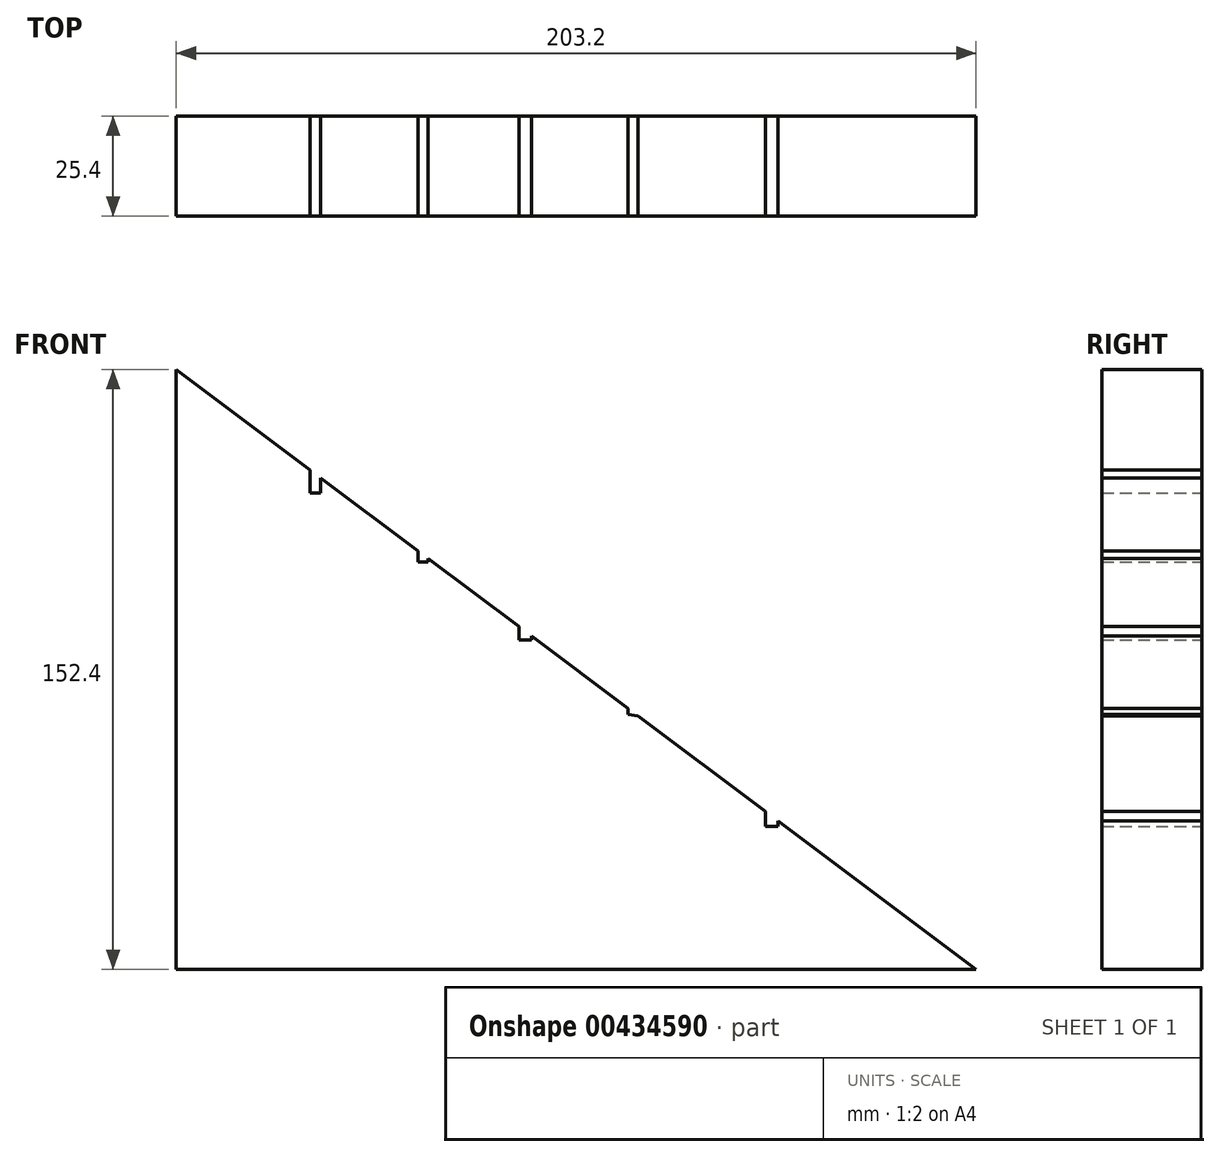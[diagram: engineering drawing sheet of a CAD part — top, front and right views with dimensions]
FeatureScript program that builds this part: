
annotation { "Feature Type Name" : "Feature", "Feature Type Description" : "" }
export const myFeature = defineFeature(function(context is Context, id is Id, definition is map)
    precondition{}
    {
        {
            var Q0;
            Q0=qCreatedBy(makeId("Front.planeOp"),FACE);
            var sketch = newSketch(context, id + "F0", { "sketchPlane" : qUnion([Q0])});
            skLineSegment(sketch, "E0", {"start": v(-68.59, 65.31) * mm, "end": v(-68.59, -87.09) * mm});
            skLineSegment(sketch, "E1", {"start": v(-68.59, -87.09) * mm, "end": v(134.61, -87.09) * mm});
            skLineSegment(sketch, "E2", {"start": v(-68.59, 65.31) * mm, "end": v(134.61, -87.09) * mm});
            skLineSegment(sketch, "E3", {"start": v(-68.59, -87.09) * mm, "end": v(81.12, -46.97) * mm});
            skLineSegment(sketch, "E4", {"start": v(-68.59, -87.09) * mm, "end": v(46.23, -20.8) * mm});
            skLineSegment(sketch, "E5", {"start": v(-68.59, -87.09) * mm, "end": v(18.5, 0) * mm});
            skLineSegment(sketch, "E6", {"start": v(-68.59, -87.09) * mm, "end": v(-7.19, 19.26) * mm});
            skLineSegment(sketch, "E7", {"start": v(-68.59, -87.09) * mm, "end": v(-34.59, 39.81) * mm});
            skLineSegment(sketch, "E8", {"start": v(-31.92, 34) * mm, "end": v(-31.92, 37.81) * mm});
            skLineSegment(sketch, "E9", {"start": v(-7.19, 19.26) * mm, "end": v(-7.19, 16.45) * mm});
            skLineSegment(sketch, "E10", {"start": v(-4.62, 16.45) * mm, "end": v(-4.62, 17.34) * mm});
            skLineSegment(sketch, "E11", {"start": v(18.5, 0) * mm, "end": v(18.5, -3.41) * mm});
            skLineSegment(sketch, "E12", {"start": v(21.69, -3.41) * mm, "end": v(21.69, -2.4) * mm});
            skLineSegment(sketch, "E13", {"start": v(46.23, -20.8) * mm, "end": v(46.23, -22.36) * mm});
            skLineSegment(sketch, "E14", {"start": v(81.12, -46.97) * mm, "end": v(81.12, -50.73) * mm});
            skLineSegment(sketch, "E15", {"start": v(84.26, -50.73) * mm, "end": v(84.26, -49.32) * mm});
            skLineSegment(sketch, "E16", {"start": v(-34.59, 39.81) * mm, "end": v(-34.59, 34) * mm});
            skLineSegment(sketch, "E17", {"start": v(-34.59, 34) * mm, "end": v(-31.92, 34) * mm});
            skLineSegment(sketch, "E18", {"start": v(-7.19, 16.45) * mm, "end": v(-4.62, 16.45) * mm});
            skLineSegment(sketch, "E19", {"start": v(18.5, -3.41) * mm, "end": v(21.69, -3.41) * mm});
            skLineSegment(sketch, "E20", {"start": v(46.23, -22.36) * mm, "end": v(48.77, -22.7) * mm});
            skLineSegment(sketch, "E21", {"start": v(84.26, -50.73) * mm, "end": v(81.12, -50.73) * mm});
            skSolve(sketch);
        }
        {
            var Q0;
            {var subQ0=sQuery(id+"F0.wireOp",EDGE,"E0");Q0=makeQuery(id+"F0.imprint","IMPRINT",FACE,{"disambiguationData":[TD([[makeQuery(id+"F0.imprint","IMPRINT",EDGE,{"derivedFrom":subQ0}),1.0]])]});}
            var Q1;
            {var subQ1=sQuery(id+"F0.wireOp",EDGE,"E1");Q1=makeQuery(id+"F0.imprint","IMPRINT",FACE,{"disambiguationData":[TD([[makeQuery(id+"F0.imprint","IMPRINT",EDGE,{"derivedFrom":subQ1}),1.0]])]});}
            var Q2;
            {var subQ1=sQuery(id+"F0.wireOp",EDGE,"E6");Q2=makeQuery(id+"F0.imprint","IMPRINT",FACE,{"disambiguationData":[TD([[makeQuery(id+"F0.imprint","IMPRINT",EDGE,{"derivedFrom":subQ1}),1.0]])]});}
            var Q3;
            {var subQ0=sQuery(id+"F0.wireOp",EDGE,"E5");Q3=makeQuery(id+"F0.imprint","IMPRINT",FACE,{"disambiguationData":[TD([[makeQuery(id+"F0.imprint","IMPRINT",EDGE,{"derivedFrom":subQ0}),1.0]])]});}
            var Q4;
            {var subQ0=sQuery(id+"F0.wireOp",EDGE,"E4");Q4=makeQuery(id+"F0.imprint","IMPRINT",FACE,{"disambiguationData":[TD([[makeQuery(id+"F0.imprint","IMPRINT",EDGE,{"derivedFrom":subQ0}),1.0]])]});}
            var Q5;
            {var subQ0=sQuery(id+"F0.wireOp",EDGE,"E3");Q5=makeQuery(id+"F0.imprint","IMPRINT",FACE,{"disambiguationData":[TD([[makeQuery(id+"F0.imprint","IMPRINT",EDGE,{"derivedFrom":subQ0}),1.0]])]});}
            extrude(context, id + "F1", {"entities" : qUnion([Q0, Q1, Q2, Q3, Q4, Q5]), "depth" : 25.4 * mm});
        }
    });
